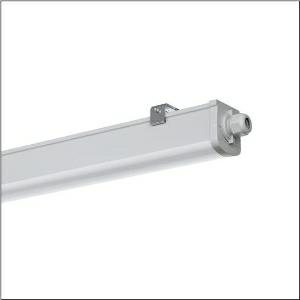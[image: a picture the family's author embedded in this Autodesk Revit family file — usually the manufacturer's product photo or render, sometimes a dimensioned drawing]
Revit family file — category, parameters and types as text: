
# Revit family: monsun_r__31_51fa20dd420b_de40
name_source: partatom
category: Lighting Fixtures
units: mm (PartAtom-declared; Revit-internal decimal feet)

## family parameters
Cut with Voids When Loaded = No
Host = Face
Light Source = No
Part Type = Normal
Room Calculation Point = No
Round Connector Dimension = Use Diameter
Shared = No

## types (1)
- Monsun® 31 (1 x LED, 2300 lm, 19 W, 4000K)
    Apparent Load = 19 VA
    CIE Flux Codes = 42 72 91 92 100
    Color Rendering = 80
    Color Temperature = 4000K
    Default Elevation = 1800 mm
    Description = Monsun® 31, damp-proof luminaire, primary optical cover: diffuser, of PC, frosted, light emission: direct distribution, primary light characteristic: symmetric, installation type: surface-mounted, LED, rated luminous flux: 2.300lm, luminous efficacy: 121lm/W, light colour: 840, colour temperature: 4000K, control gear: ECG, with terminal, 5+1-pole, max. 2.5mm², through-wiring: 3x 2.5mm² + 3x 1.5mm², mains connection: 220..240V, AC, 50/60Hz, rated input power: 19W, housing, luminaire housing, of PC, light grey (RAL 7035), length: 558mm, width: 68mm, height: 76mm, protection rating (complete): IP66, insulation class (complete): insulation class II (safety insulation), certification: CE, ENEC, UKCA, protection symbol: D, impact resistance: IK08, permissible operating ambient temperature: -20..+40°C, corresponds to IFS (International Featured Standards) requirements for safety and quality in the food industry, packaging unit: 1 piece
    Height = 77 mm
    Lamp = 1 x LED
    Lamp Light Flux = 2300 lm
    Lamp Power = 19 W
    Lamp count = 1
    Length = 618 mm
    Luminous efficacy = 121 lm/W
    Manufacturer = Siteco
    ModVariant = No
    Model = 51FA20DD420B
    Mounting Place = Ceiling
    Mounting Type = Surface mounted
    Number of Poles = 1
    OnlyDefault = Yes
    Power Factor = 1
    Product Name = Monsun® 31
    Product group = damp-proof luminaire | ceiling mounted
    ProductGroupID = 300
    Protection Class = Protection class II
    Protection Degree = IP 66
    RLX_Detail_Level = 1
    RlxData = <blob elided: 32629 chars, md5=570ec0f7>
    Socket = socket
    Standby Power = 0 W
    System Light Flux = 2300 lm
    System Power = 19 W
    Type Comments = Product without accessories
    Type Image = l_1006174.jpg
    URL = http://relux.com
    VarID = ---
    Voltage = 0 V
    Weight = 0.00 kg
    Width = 69 mm

## geometry (parser evidence)
native form markers: Blend x4, Sweep x11
no freeform markers — native parametric forms only
